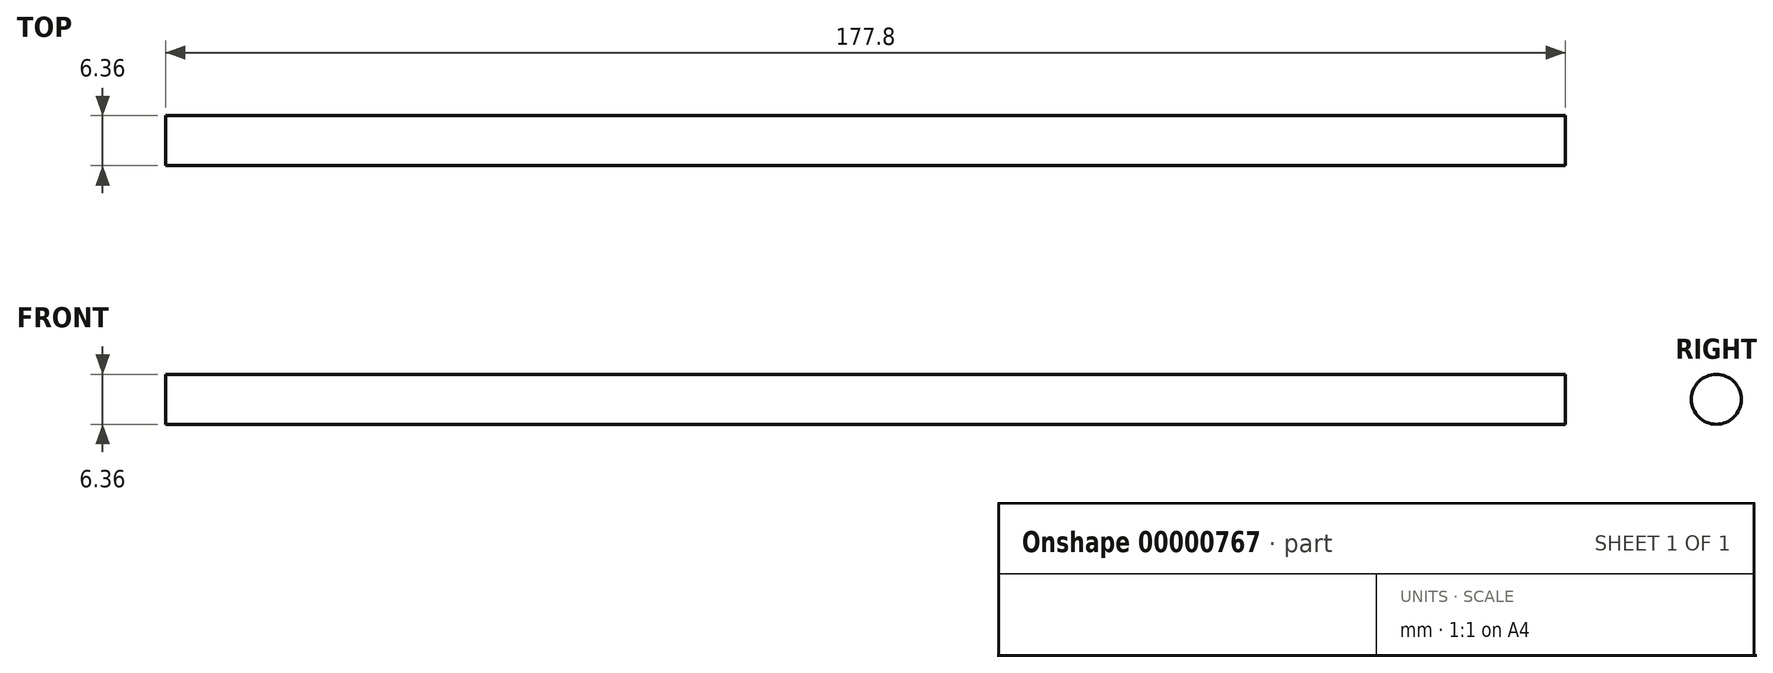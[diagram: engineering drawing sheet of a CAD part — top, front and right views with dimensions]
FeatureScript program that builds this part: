
annotation { "Feature Type Name" : "Feature", "Feature Type Description" : "" }
export const myFeature = defineFeature(function(context is Context, id is Id, definition is map)
    precondition{}
    {
        {
            var Q0;
            Q0 = qCreatedBy(makeId("Right.planeOp"), FACE);
            var sketch = newSketch(context, id + "F0", { "sketchPlane" : qUnion([Q0])});
            skCircle(sketch, "E0", {"center": v(0, 0) * mm, "radius": 3.18 * mm});
            skSolve(sketch);
        }
        {
            var Q0;
            Q0=makeQuery(id+"F0.imprint","IMPRINT",FACE,{"disambiguationData":[TD([[makeQuery(id+"F0.imprint","IMPRINT",EDGE,{"derivedFrom":sQuery(id+"F0.wireOp",EDGE,"E0")}),1.0]])]});
            extrude(context, id + "F1", {"entities" : qUnion([Q0]), "endBound" : BoundingType.SYMMETRIC, "depth" : 177.8 * mm});
        }
    });
